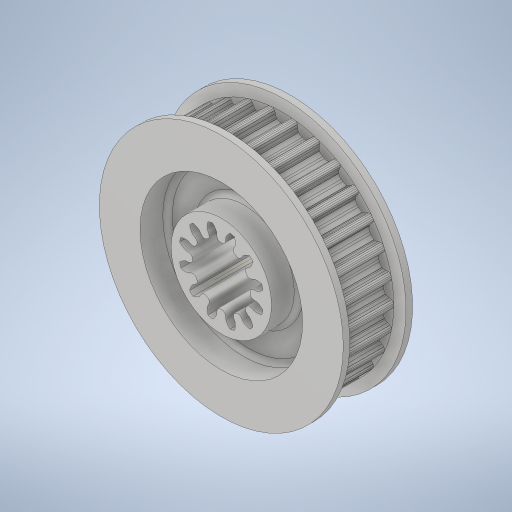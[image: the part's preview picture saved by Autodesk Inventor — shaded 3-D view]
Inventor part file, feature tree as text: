
AUTODESK INVENTOR PART (.ipt)
format: ipt  version: 2023 (Build 270158000, 158)  size: 1,963,008 bytes
history: native  units: in
note: dims shown in document units (in); Inventor stores cm internally (conversion verified against a paired STEP export)
features: extrude x2, mirror x2, projected_geometry x2, sketch x1, other x1, boolean_combine x1
ambient origin geometry x8: Origin, YZ Plane, XZ Plane, XY Plane, X Axis, Y Axis, Z Axis, Center Point
bodies: Solid1 (feature_tree), Solid2 (feature_tree)
feature tree (9):
  sketch  "Sketch1"  dims[d0=0.3937in d1=0.0in d2=0.3937in d3=0.0in d4=0.3937in]
  extrude  "Extrusion1"  Depth=0.3937in TaperAngle=0.0deg
  extrude  "Extrusion2"  Depth=0.3937in
  other  "Cut-Extrude2"
  boolean_combine  "Combine1"
  mirror  "Mirror2"
  projected_geometry  "Projected Loop1"
  projected_geometry  "Projected Loop2"
  mirror  "Mirror1"
